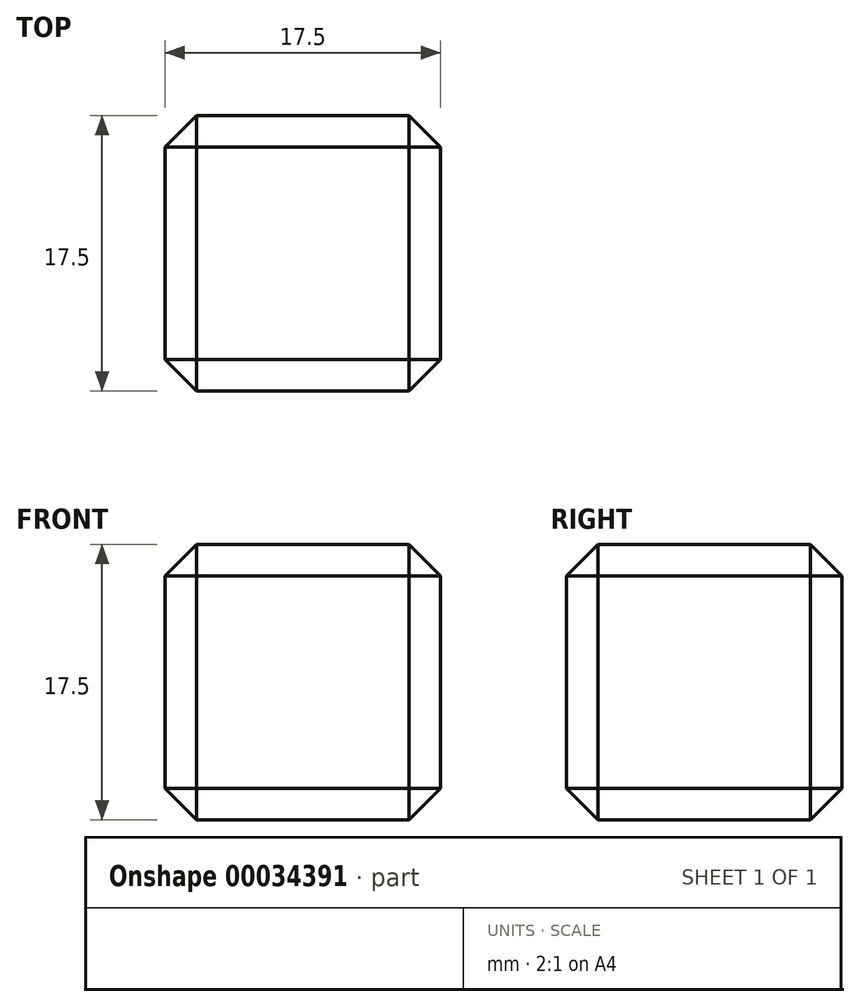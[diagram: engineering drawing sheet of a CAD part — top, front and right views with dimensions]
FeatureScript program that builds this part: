
annotation { "Feature Type Name" : "Feature", "Feature Type Description" : "" }
export const myFeature = defineFeature(function(context is Context, id is Id, definition is map)
    precondition{}
    {
        {
            var Q0;
            Q0=qCreatedBy(makeId("Top.planeOp"),FACE);
            var sketch = newSketch(context, id + "F0", { "sketchPlane" : qUnion([Q0])});
            skLineSegment(sketch, "E0.rect.bottom", {"start": v(8.75, 8.75) * mm, "end": v(-8.75, 8.75) * mm});
            skLineSegment(sketch, "E0.rect.top", {"start": v(8.75, -8.75) * mm, "end": v(-8.75, -8.75) * mm});
            skLineSegment(sketch, "E0.rect.left", {"start": v(8.75, 8.75) * mm, "end": v(8.75, -8.75) * mm});
            skLineSegment(sketch, "E0.rect.right", {"start": v(-8.75, 8.75) * mm, "end": v(-8.75, -8.75) * mm});
            skPoint(sketch, "E0.rect.middle", {"position": v(0, 0) * mm});
            skSolve(sketch);
        }
        {
            var Q0;
            Q0 = qSketchRegion(id + "F0", true);
            extrude(context, id + "F1", {"entities" : qUnion([Q0]), "endBound" : BoundingType.SYMMETRIC, "depth" : 17.5 * mm});
        }
        {
            var Q0;
            Q0=makeQuery(id+"F1.opExtrude","CAP_EDGE",EDGE,{"disambiguationData":[OSD([sQuery(id+"F0.wireOp",EDGE,"E0.rect.right")])],"isStart":false});
            var Q1;
            Q1=makeQuery(id+"F1.opExtrude","CAP_EDGE",EDGE,{"disambiguationData":[OSD([sQuery(id+"F0.wireOp",EDGE,"E0.rect.top")])],"isStart":false});
            var Q2;
            Q2=makeQuery(id+"F1.opExtrude","CAP_EDGE",EDGE,{"disambiguationData":[OSD([sQuery(id+"F0.wireOp",EDGE,"E0.rect.left")])],"isStart":false});
            var Q3;
            Q3=makeQuery(id+"F1.opExtrude","CAP_EDGE",EDGE,{"disambiguationData":[OSD([sQuery(id+"F0.wireOp",EDGE,"E0.rect.bottom")])],"isStart":false});
            var Q4;
            Q4=makeQuery(id+"F1.opExtrude","SWEPT_EDGE",EDGE,{"disambiguationData":[OSD([sQuery(id+"F0.wireOp",EDGE,"E0.rect.top"),sQuery(id+"F0.wireOp",EDGE,"E0.rect.left")])]});
            var Q5;
            Q5=makeQuery(id+"F1.opExtrude","SWEPT_EDGE",EDGE,{"disambiguationData":[OSD([sQuery(id+"F0.wireOp",EDGE,"E0.rect.bottom"),sQuery(id+"F0.wireOp",EDGE,"E0.rect.left")])]});
            var Q6;
            Q6=makeQuery(id+"F1.opExtrude","CAP_EDGE",EDGE,{"disambiguationData":[OSD([sQuery(id+"F0.wireOp",EDGE,"E0.rect.left")])],"isStart":true});
            var Q7;
            Q7=makeQuery(id+"F1.opExtrude","CAP_EDGE",EDGE,{"disambiguationData":[OSD([sQuery(id+"F0.wireOp",EDGE,"E0.rect.bottom")])],"isStart":true});
            var Q8;
            Q8=makeQuery(id+"F1.opExtrude","SWEPT_EDGE",EDGE,{"disambiguationData":[OSD([sQuery(id+"F0.wireOp",EDGE,"E0.rect.bottom"),sQuery(id+"F0.wireOp",EDGE,"E0.rect.right")])]});
            var Q9;
            Q9=makeQuery(id+"F1.opExtrude","SWEPT_EDGE",EDGE,{"disambiguationData":[OSD([sQuery(id+"F0.wireOp",EDGE,"E0.rect.top"),sQuery(id+"F0.wireOp",EDGE,"E0.rect.right")])]});
            var Q10;
            Q10=makeQuery(id+"F1.opExtrude","CAP_EDGE",EDGE,{"disambiguationData":[OSD([sQuery(id+"F0.wireOp",EDGE,"E0.rect.top")])],"isStart":true});
            var Q11;
            Q11=makeQuery(id+"F1.opExtrude","CAP_EDGE",EDGE,{"disambiguationData":[OSD([sQuery(id+"F0.wireOp",EDGE,"E0.rect.right")])],"isStart":true});
            chamfer(context, id + "F2", {"entities" : qUnion([Q0, Q1, Q2, Q3, Q4, Q5, Q6, Q7, Q8, Q9, Q10, Q11]), "width" : 2 * mm, "tangentPropagation" : true});
        }
    });
